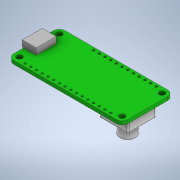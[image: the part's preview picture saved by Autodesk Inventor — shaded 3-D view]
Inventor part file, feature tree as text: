
AUTODESK INVENTOR PART (.ipt)
format: ipt  version: 2021 (Build 250183000, 183)  size: 246,272 bytes
history: native  units: in
note: dims shown in document units (in); Inventor stores cm internally (conversion verified against a paired STEP export)
features: extrude x7, sketch x7, pattern_linear x2, fillet x1, projected_geometry x1
ambient origin geometry x8: Origin, YZ Plane, XZ Plane, XY Plane, X Axis, Y Axis, Z Axis, Center Point
bodies: Solid1 (feature_tree)
feature tree (18):
  extrude  "Extrusion1"  Depth=0.9in
  extrude  "Extrusion4"  Depth=0.7in
  extrude  "Extrusion6"  Depth=0.1in
  pattern_linear  "Rectangular Pattern1"  Spacing1=0.063in  [1 undecoded]
  extrude  "Extrusion7"  Depth=0.025in
  pattern_linear  "Rectangular Pattern2"  Spacing1=0.245in  [1 undecoded]
  extrude  "Extrusion8"  Depth=0.11in TaperAngle=0.0deg
  extrude  "Extrusion9"  Depth=0.1181in
  fillet  "Fillet2"  Radius=0.05in
  extrude  "Extrusion10"  Depth=0.05in
  sketch  "Sketch1"  dims[d0=2.0in d1=0.9in]
  sketch  "Sketch4"  dims[d2=0.1in d6=0.7in]
  sketch  "Sketch6"  dims[d9=0.35in d10=0.1in]
  sketch  "Sketch7"  dims[d11=0.1in]
  sketch  "Sketch8"  dims[d13=0.1in]
  sketch  "Sketch9"  dims[d14=0.1in]
  sketch  "Sketch10"  dims[d15=0.1in d16=0.063in d17=0.0in d34=0.025in d35=0.245in d38=0.11in d39=0.0in d46=0.0394in d47=0.05in d48=0.05in d49=0.0in d50=0.0in d51=6.2992in d53=0.1in d54=1.15in d55=0.05in d56=0.0394in d57=0.0in d58=0.0in d59=4.7244in d61=0.1in d62=0.35in d63=0.5in d64=1.65in d65=0.2638in d66=0.0in d67=0.28in d69=0.25in d70=0.0in d71=0.025in d72=0.32in d74=0.525in d75=0.1181in d76=0.0in]
  projected_geometry  "Project Cut Edges1"
note: 2 required parameter values undecoded (feature->parameter linkage not recoverable at this tier; creation-order binding heuristic only, values carry confidence <= 0.55)
